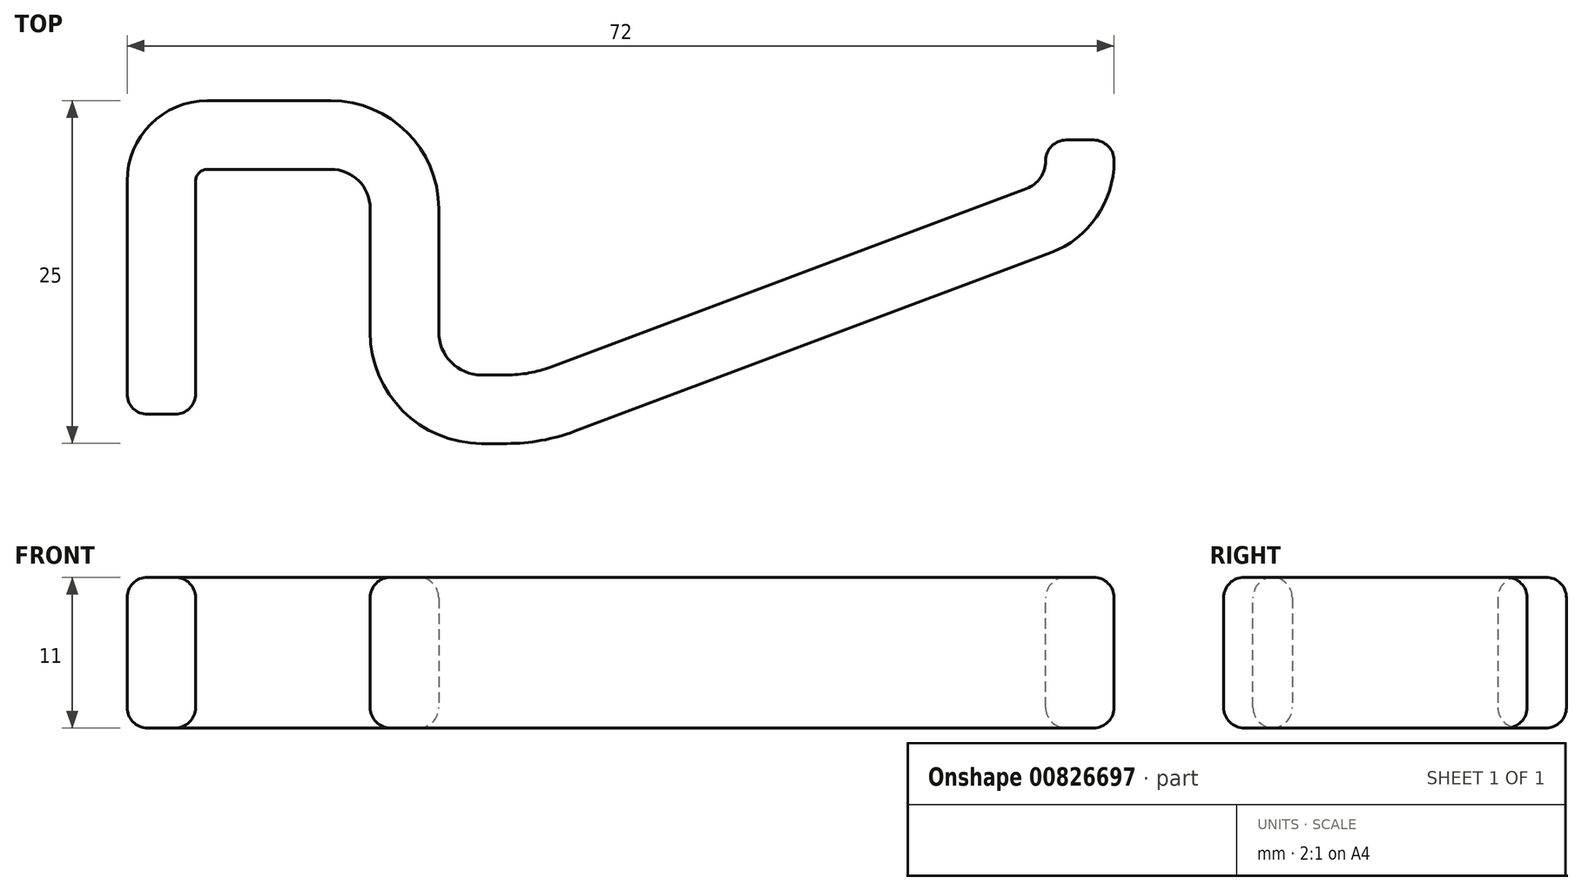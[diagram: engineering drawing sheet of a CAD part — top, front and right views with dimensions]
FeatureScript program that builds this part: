
annotation { "Feature Type Name" : "Feature", "Feature Type Description" : "" }
export const myFeature = defineFeature(function(context is Context, id is Id, definition is map)
    precondition{}
    {
        {
            var Q0;
            Q0=qCreatedBy(makeId("Top.planeOp"),FACE);
            var sketch = newSketch(context, id + "F0", { "sketchPlane" : qUnion([Q0])});
            skLineSegment(sketch, "E0", {"start": v(-10.82, 0) * mm, "end": v(-10.82, 17) * mm});
            skLineSegment(sketch, "E1", {"start": v(-7.82, 20) * mm, "end": v(1.18, 20) * mm});
            skLineSegment(sketch, "E2", {"start": v(6.18, 15) * mm, "end": v(6.18, 6) * mm});
            skLineSegment(sketch, "E3", {"start": v(12.18, 0) * mm, "end": v(14, 0) * mm});
            skLineSegment(sketch, "E4", {"start": v(18.21, 0.76) * mm, "end": v(52.93, 13.78) * mm});
            skLineSegment(sketch, "E5", {"start": v(56.18, 18.47) * mm, "end": v(56.18, 20) * mm});
            skPoint(sketch, "E6.visualSharp", {"position": v(-10.82, 20) * mm});
            skArc(sketch, "E6.filletArc", {"start": v(-7.82, 20) * mm, "mid": v(-9.95, 19.12) * mm, "end": v(-10.82, 17) * mm});
            skPoint(sketch, "E7.visualSharp", {"position": v(6.18, 20) * mm});
            skArc(sketch, "E7.filletArc", {"start": v(6.18, 15) * mm, "mid": v(4.71, 18.54) * mm, "end": v(1.18, 20) * mm});
            skPoint(sketch, "E8.visualSharp", {"position": v(6.18, 0) * mm});
            skArc(sketch, "E8.filletArc", {"start": v(6.18, 6) * mm, "mid": v(7.93, 1.76) * mm, "end": v(12.18, 0) * mm});
            skPoint(sketch, "E9.visualSharp", {"position": v(16.18, 0) * mm});
            skArc(sketch, "E9.filletArc", {"start": v(14, 0) * mm, "mid": v(16.14, 0.2) * mm, "end": v(18.21, 0.76) * mm});
            skPoint(sketch, "E10.visualSharp", {"position": v(56.18, 15) * mm});
            skArc(sketch, "E10.filletArc", {"start": v(52.93, 13.78) * mm, "mid": v(55.29, 15.62) * mm, "end": v(56.18, 18.47) * mm});
            skSolve(sketch);
        }
        {
            var Q0;
            Q0=qCreatedBy(makeId("Front.planeOp"),FACE);
            var sketch = newSketch(context, id + "F1", { "sketchPlane" : qUnion([Q0])});
            skLineSegment(sketch, "E11.bottom", {"start": v(-13.7, 5.5) * mm, "end": v(-8.7, 5.5) * mm});
            skLineSegment(sketch, "E11.top", {"start": v(-13.7, -5.5) * mm, "end": v(-8.7, -5.5) * mm});
            skLineSegment(sketch, "E11.left", {"start": v(-13.7, 5.5) * mm, "end": v(-13.7, -5.5) * mm});
            skLineSegment(sketch, "E11.right", {"start": v(-8.7, 5.5) * mm, "end": v(-8.7, -5.5) * mm});
            skSolve(sketch);
        }
        {
            var Q0;
            Q0=makeQuery(id+"F1.imprint","IMPRINT",FACE,{"disambiguationData":[TD([[makeQuery(id+"F1.imprint","IMPRINT",EDGE,{"derivedFrom":sQuery(id+"F1.wireOp",EDGE,"E11.bottom")}),-1.0]])]});
            var Q1;
            Q1=sQuery(id+"F0.wireOp",EDGE,"E0");
            var Q2;
            Q2=sQuery(id+"F0.wireOp",EDGE,"E6.filletArc");
            var Q3;
            Q3=sQuery(id+"F0.wireOp",EDGE,"E1");
            var Q4;
            Q4=sQuery(id+"F0.wireOp",EDGE,"E7.filletArc");
            var Q5;
            Q5=sQuery(id+"F0.wireOp",EDGE,"E2");
            var Q6;
            Q6=sQuery(id+"F0.wireOp",EDGE,"E8.filletArc");
            var Q7;
            Q7=sQuery(id+"F0.wireOp",EDGE,"E3");
            var Q8;
            Q8=sQuery(id+"F0.wireOp",EDGE,"E9.filletArc");
            var Q9;
            Q9=sQuery(id+"F0.wireOp",EDGE,"E4");
            var Q10;
            Q10=sQuery(id+"F0.wireOp",EDGE,"E10.filletArc");
            var Q11;
            Q11=sQuery(id+"F0.wireOp",EDGE,"E5");
            sweep(context, id + "F2", {"profiles" : qUnion([Q0]), "path" : qUnion([Q1, Q2, Q3, Q4, Q5, Q6, Q7, Q8, Q9, Q10, Q11])});
        }
        {
            var Q0;
            Q0=makeQuery(id+"F2.opSweep","SWEPT_FACE",FACE,{"disambiguationData":[OSD([sQuery(id+"F0.wireOp",EDGE,"E0"),sQuery(id+"F1.wireOp",EDGE,"E11.bottom")])]});
            var Q1;
            Q1=makeQuery(id+"F2.opSweep","SWEPT_FACE",FACE,{"disambiguationData":[OSD([sQuery(id+"F0.wireOp",EDGE,"E0"),sQuery(id+"F1.wireOp",EDGE,"E11.top")])]});
            var Q2;
            Q2=makeQuery(id+"F2.opSweep","CAP_FACE",FACE,{"disambiguationData":[OSD([sQuery(id+"F0.wireOp",VERTEX,"E0.start"),sQuery(id+"F1.wireOp",EDGE,"E11.bottom"),sQuery(id+"F1.wireOp",EDGE,"E11.top"),sQuery(id+"F1.wireOp",EDGE,"E11.left"),sQuery(id+"F1.wireOp",EDGE,"E11.right")])],"isStart":true});
            var Q3;
            Q3=makeQuery(id+"F2.opSweep","CAP_FACE",FACE,{"disambiguationData":[OSD([sQuery(id+"F0.wireOp",VERTEX,"E5.end"),sQuery(id+"F1.wireOp",EDGE,"E11.bottom"),sQuery(id+"F1.wireOp",EDGE,"E11.top"),sQuery(id+"F1.wireOp",EDGE,"E11.left"),sQuery(id+"F1.wireOp",EDGE,"E11.right")])],"isStart":false});
            fillet(context, id + "F3", {"entities" : qUnion([Q0, Q1, Q2, Q3]), "radius" : 1.5 * mm, "tangentPropagation" : true, "allowEdgeOverflow" : false});
        }
    });
